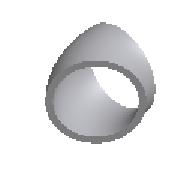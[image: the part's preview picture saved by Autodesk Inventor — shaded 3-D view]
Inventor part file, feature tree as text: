
AUTODESK INVENTOR PART (.ipt)
format: ipt  version: 2023 (Build 270158000, 158)  size: 174,592 bytes
history: native  units: mm (DEFAULTED — no unit token found)
features: other x4, sketch x2, sweep x1
ambient origin geometry x8: Origin, YZ Plane, XZ Plane, XY Plane, X Axis, Y Axis, Z Axis, Center Point
bodies: Solid1 (feature_tree)
feature tree (7):
  sweep  "Sweep1"
  other  "Work Point1"
  other  "Work Point2"
  other  "Work Axis1"
  other  "Work Axis2"
  sketch  "Sketch1"  dims[d0=318.1mm d1=323.9mm]
  sketch  "Sketch2"  dims[d2=126.0mm d3=45.0deg d4=126.0mm d5=0.0mm d6=0.0mm]
